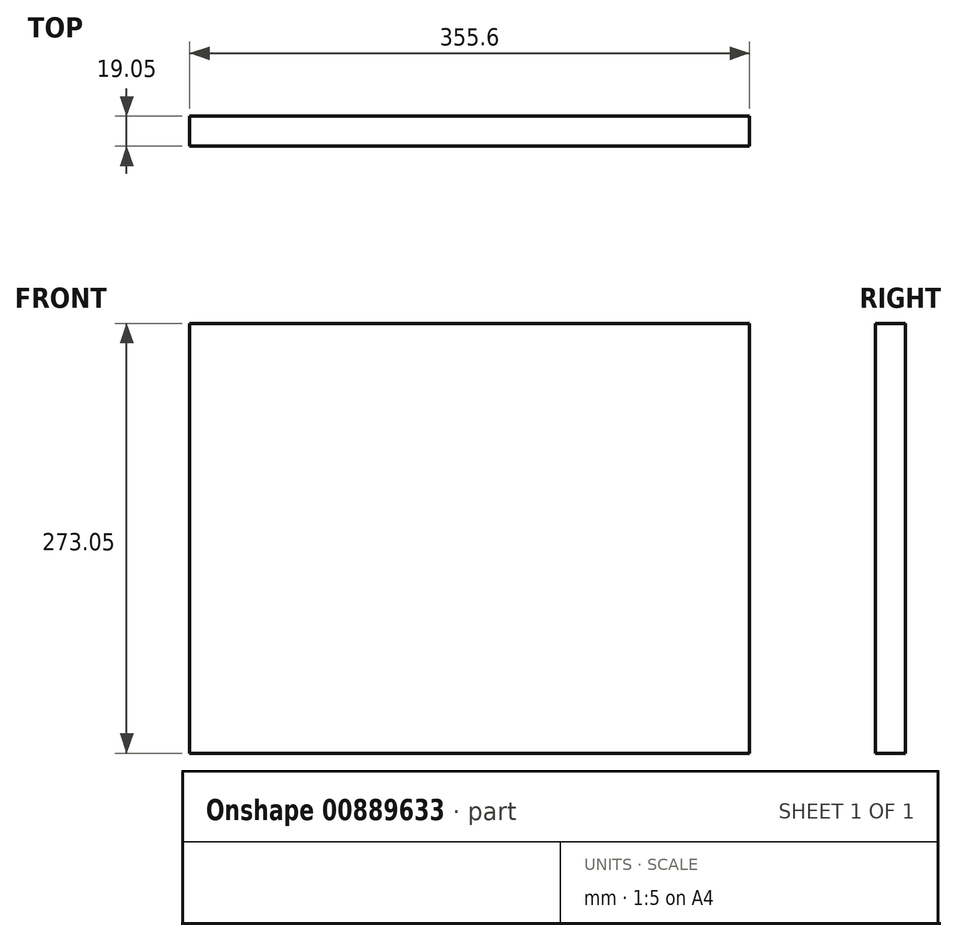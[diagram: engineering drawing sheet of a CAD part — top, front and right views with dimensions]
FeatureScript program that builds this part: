
annotation { "Feature Type Name" : "Feature", "Feature Type Description" : "" }
export const myFeature = defineFeature(function(context is Context, id is Id, definition is map)
    precondition{}
    {
        {
            var Q0;
            Q0=qCreatedBy(makeId("Front.planeOp"),FACE);
            var sketch = newSketch(context, id + "F0", { "sketchPlane" : qUnion([Q0])});
            skLineSegment(sketch, "E0.bottom", {"start": v(0, 0) * mm, "end": v(355.6, 0) * mm});
            skLineSegment(sketch, "E0.top", {"start": v(0, 273.05) * mm, "end": v(355.6, 273.05) * mm});
            skLineSegment(sketch, "E0.left", {"start": v(0, 0) * mm, "end": v(0, 273.05) * mm});
            skLineSegment(sketch, "E0.right", {"start": v(355.6, 0) * mm, "end": v(355.6, 273.05) * mm});
            skSolve(sketch);
        }
        {
            var Q0;
            Q0 = qSketchRegion(id + "F0", true);
            extrude(context, id + "F1", {"entities" : qUnion([Q0]), "depth" : 19.05 * mm, "offsetDistance" : 25.4 * mm});
        }
    });
